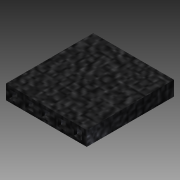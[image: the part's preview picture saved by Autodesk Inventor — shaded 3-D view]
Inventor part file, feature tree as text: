
AUTODESK INVENTOR PART (.ipt)
format: ipt  version: 2014 (Build 180170000, 170)  size: 169,472 bytes
history: native  units: in
note: dims shown in document units (in); Inventor stores cm internally (conversion verified against a paired STEP export)
features: extrude x4, sketch x4, chamfer x1, pattern_linear x1, projected_geometry x1
ambient origin geometry x8: Origin, YZ Plane, XZ Plane, XY Plane, X Axis, Y Axis, Z Axis, Center Point
bodies: Solid1 (feature_tree)
feature tree (11):
  extrude  "Extrusion1"  Depth=0.54in
  extrude  "Extrusion2"  Depth=0.03in
  chamfer  "Chamfer1"  Distance=0.03in
  extrude  "Extrusion3"  Depth=0.5in TaperAngle=0.0deg
  extrude  "Extrusion4"  Depth=0.01in TaperAngle=45.0deg
  pattern_linear  "Rectangular Pattern1"  Count1=5 Spacing1=0.1in
  sketch  "Sketch1"  dims[d0=0.5in d1=0.54in]
  sketch  "Sketch2"  dims[d2=0.09in d3=0.0in d4=0.03in]
  sketch  "Sketch3"  dims[d5=0.03in]
  projected_geometry  "Projected Loop1"
  sketch  "Sketch4"  dims[d6=0.03in d7=0.03in d8=0.5in d9=0.0in d10=0.01in d11=0.125in d12=45.0deg d13=1.9685in d15=0.1in d16=0.0255in d17=0.0in d18=0.02in d19=0.05in d20=0.05in d21=0.15in d22=0.005in d23=0.0in]
